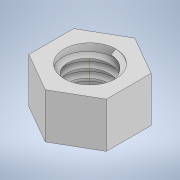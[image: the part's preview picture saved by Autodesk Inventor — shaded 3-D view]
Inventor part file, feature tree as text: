
AUTODESK INVENTOR PART (.ipt)
format: ipt  version: 2021.1 (Build 251245000, 245)  size: 203,264 bytes
history: native  units: in
note: dims shown in document units (in); Inventor stores cm internally (conversion verified against a paired STEP export)
features: sketch x3, extrude x2, helix x1
ambient origin geometry x8: Origin, YZ Plane, XZ Plane, XY Plane, X Axis, Y Axis, Z Axis, Center Point
bodies: Solid1 (feature_tree)
feature tree (6):
  extrude  "Extrusion1"  Depth=0.3281in TaperAngle=0.0deg
  extrude  "Extrusion2"  TaperAngle=0.0deg  [1 undecoded]
  helix  "Coil2"  [1 undecoded]
  sketch  "Sketch1"  dims[d0=0.5625in d1=0.3281in d2=0.0in]
  sketch  "Sketch2"  dims[d3=0.375in d4=0.0in d5=0.0in d18=60.0deg]
  sketch  "Sketch3"  dims[d19=0.1535in d20=30.0deg d21=0.0625in d22=0.2891in d23=0.3937in d24=0.0in d25=90.0deg d26=90.0deg d27=0.0in d28=0.0in]
note: 2 required parameter values undecoded (feature->parameter linkage not recoverable at this tier; creation-order binding heuristic only, values carry confidence <= 0.55)
